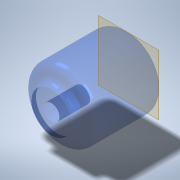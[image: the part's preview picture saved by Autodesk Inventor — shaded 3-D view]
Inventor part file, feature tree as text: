
AUTODESK INVENTOR PART (.ipt)
format: ipt  version: 2021 (Build 250183000, 183)  size: 179,200 bytes
history: native  units: mm
features: other x4, extrude x3, fillet x3, sketch x3, reference x2, chamfer x1
ambient origin geometry x8: Origin, YZ Plane, XZ Plane, XY Plane, X Axis, Y Axis, Z Axis, Center Point
bodies: Body1 (feature_tree)
feature tree (16):
  other  "Bryła1"
  other  "Płaszczyzna konstrukcyjna1"
  extrude  "Wyciągnięcie proste1"  Depth=310.0mm TaperAngle=0.0deg
  fillet  "Zaokrąglenie1"  Radius=30.0mm
  extrude  "Wyciągnięcie proste2"  Depth=160.0mm
  fillet  "Zaokrąglenie2"  Radius=30.0mm
  fillet  "Zaokrąglenie3"  Radius=30.0mm
  extrude  "Wyciągnięcie proste3"  Depth=20.0mm
  chamfer  "Faza1"  Distance=65.0mm
  sketch  "Szkic1"
  reference  "Odniesienie1"
  reference  "Odniesienie2"
  sketch  "Szkic2"
  sketch  "Szkic3"
  other  "wszystko.iam"
  other  "garnek:1"
